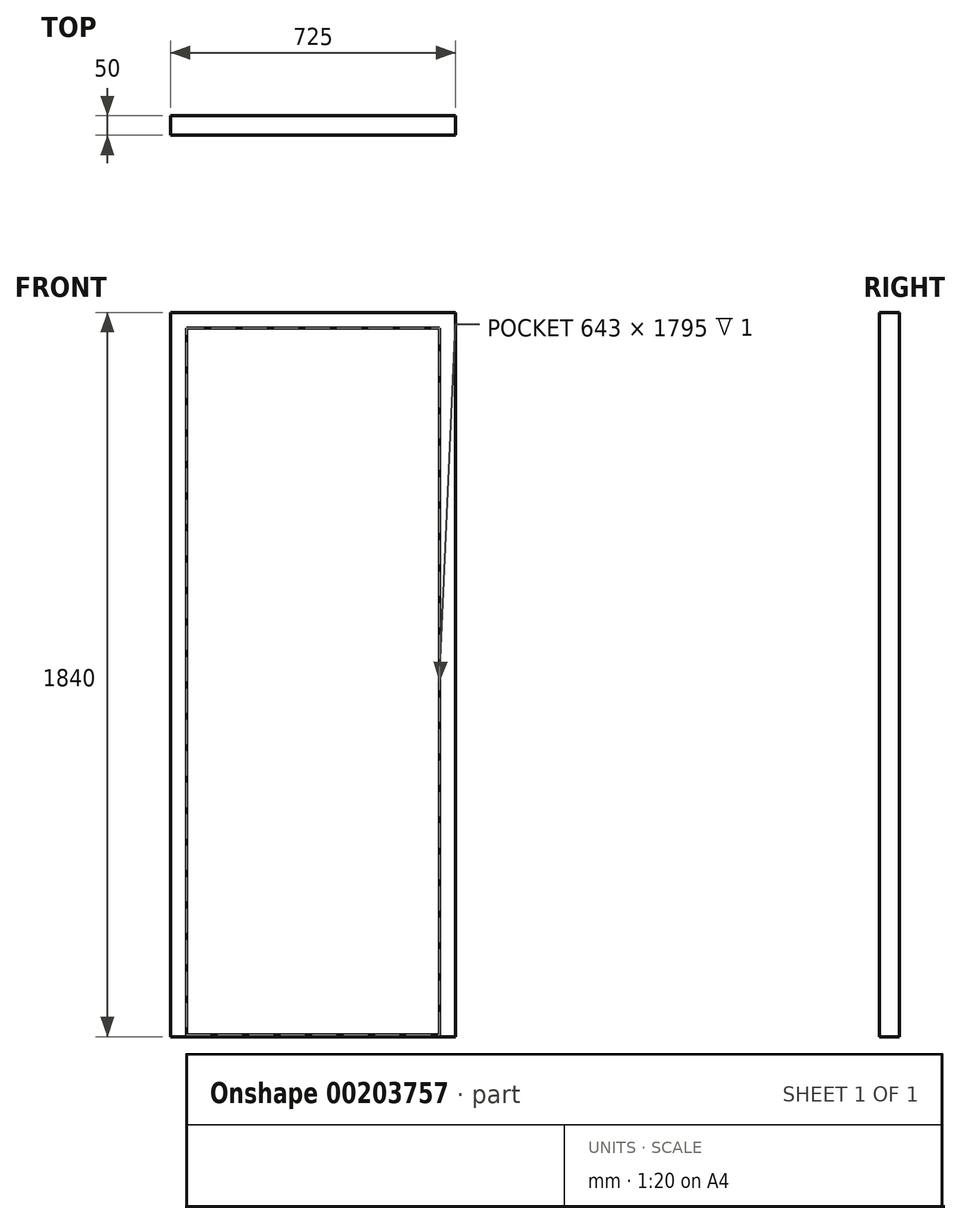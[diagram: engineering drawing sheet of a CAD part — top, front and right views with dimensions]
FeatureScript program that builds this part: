
annotation { "Feature Type Name" : "Feature", "Feature Type Description" : "" }
export const myFeature = defineFeature(function(context is Context, id is Id, definition is map)
    precondition{}
    {
        {
            var Q0;
            Q0=qCreatedBy(makeId("Front.planeOp"),FACE);
            var sketch = newSketch(context, id + "F0", { "sketchPlane" : qUnion([Q0])});
            skLineSegment(sketch, "E0.bottom", {"start": v(362.5, -920) * mm, "end": v(-362.5, -920) * mm});
            skLineSegment(sketch, "E0.top", {"start": v(362.5, 920) * mm, "end": v(-362.5, 920) * mm});
            skLineSegment(sketch, "E0.left", {"start": v(362.5, -920) * mm, "end": v(362.5, 920) * mm});
            skLineSegment(sketch, "E0.right", {"start": v(-362.5, -920) * mm, "end": v(-362.5, 920) * mm});
            skPoint(sketch, "E0.middle", {"position": v(0, 0) * mm});
            skSolve(sketch);
        }
        {
            var Q0;
            Q0 = qSketchRegion(id + "F0", true);
            extrude(context, id + "F1", {"entities" : qUnion([Q0]), "depth" : 50 * mm});
        }
        {
            var Q0;
            Q0=makeQuery(id+"F1.opExtrude","CAP_FACE",FACE,{"disambiguationData":[OSD([sQuery(id+"F0.wireOp",EDGE,"E0.bottom"),sQuery(id+"F0.wireOp",EDGE,"E0.top"),sQuery(id+"F0.wireOp",EDGE,"E0.left"),sQuery(id+"F0.wireOp",EDGE,"E0.right")])],"isStart":false});
            var sketch = newSketch(context, id + "F2", { "sketchPlane" : qUnion([Q0])});
            skLineSegment(sketch, "E1", {"start": v(0, 920) * mm, "end": v(0, -920) * mm, "construction": true});
            skLineSegment(sketch, "E2.bottom", {"start": v(321.5, -915) * mm, "end": v(-321.5, -915) * mm});
            skLineSegment(sketch, "E2.top", {"start": v(321.5, 880) * mm, "end": v(-321.5, 880) * mm});
            skLineSegment(sketch, "E2.left", {"start": v(321.5, -915) * mm, "end": v(321.5, 880) * mm});
            skLineSegment(sketch, "E2.right", {"start": v(-321.5, -915) * mm, "end": v(-321.5, 880) * mm});
            skPoint(sketch, "E2.middle", {"position": v(0, -17.5) * mm});
            skSolve(sketch);
        }
        {
            var Q0;
            Q0 = qSketchRegion(id + "F2", true);
            extrude(context, id + "F3", {"entities" : qUnion([Q0]), "operationType" : NewBodyOperationType.REMOVE, "oppositeDirection" : true, "depth" : 1 * mm});
        }
    });
